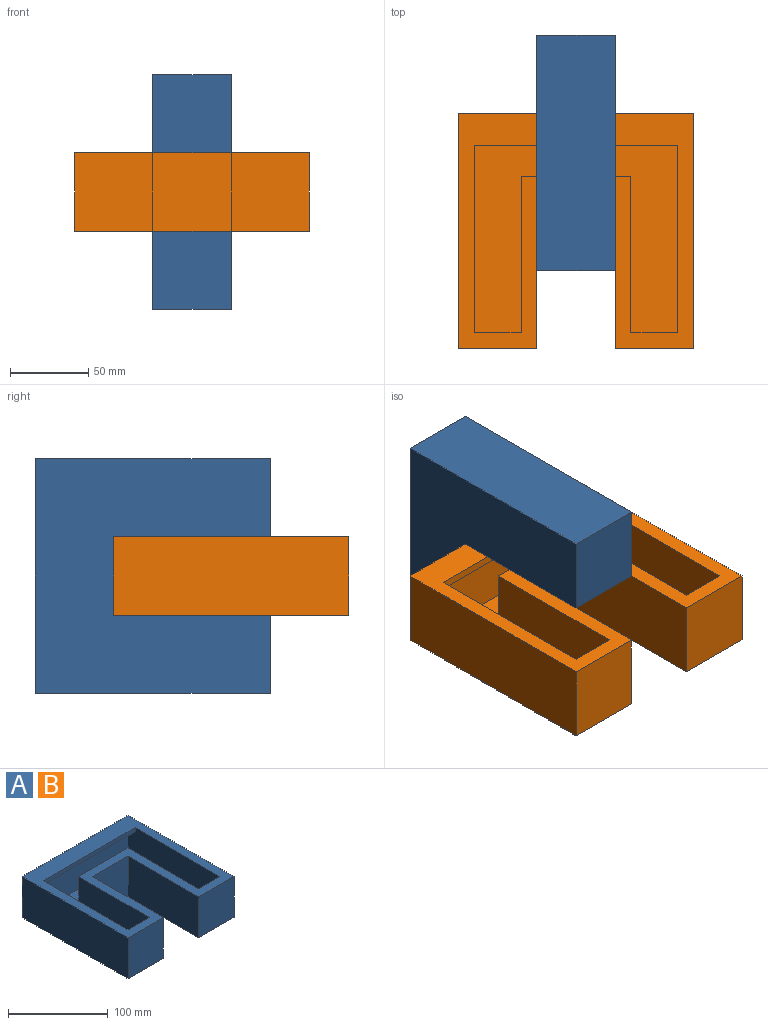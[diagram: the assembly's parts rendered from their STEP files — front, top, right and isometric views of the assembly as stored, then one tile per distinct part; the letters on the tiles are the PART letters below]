
ASSEMBLY  parts=2 mates=1
PART A: 21 faces, bbox 150x150x50 mm
  f0: plane 130x40mm, normal (0,-1,0), area 5200mm2, adj f1,f10,f18,f19
  f1: plane 130x45mm, normal (-1,0,0), area 5800mm2, adj f0,f11,f17,f18,f19,f20
  f2: plane 150x150mm, normal (0,0,-1), area 17500mm2, adj f3,f4,f5,f6,f7,f8,f9,f16
  f3: plane 150x50mm, normal (-1,0,0), area 7500mm2, adj f2,f4,f16,f17
  f4: plane 50x50mm, normal (0,-1,0), area 2500mm2, adj f2,f3,f5,f17
  f5: plane 100x50mm, normal (1,0,0), area 5000mm2, adj f2,f4,f6,f17
  f6: plane 50x50mm, normal (0,-1,0), area 2500mm2, adj f2,f5,f7,f17
  f7: plane 100x50mm, normal (-1,0,0), area 5000mm2, adj f2,f6,f8,f17
  f8: plane 50x50mm, normal (0,-1,0), area 2500mm2, adj f2,f7,f9,f17
  f9: plane 150x50mm, normal (1,0,0), area 7500mm2, adj f2,f8,f16,f17
  f10: plane 130x45mm, normal (1,0,0), area 5800mm2, adj f0,f15,f17,f18,f19,f20
  f11: plane 45x30mm, normal (0,1,0), area 1350mm2, adj f1,f12,f17,f18
  f12: plane 100x45mm, normal (1,0,0), area 4500mm2, adj f11,f13,f17,f18
  f13: plane 70x45mm, normal (0,1,0), area 3150mm2, adj f12,f14,f17,f18
  f14: plane 100x45mm, normal (-1,0,0), area 4500mm2, adj f13,f15,f17,f18
  f15: plane 45x30mm, normal (0,1,0), area 1350mm2, adj f10,f14,f17,f18
  f16: plane 150x50mm, normal (0,1,0), area 7500mm2, adj f2,f3,f9,f17
  f17: plane 150x150mm, normal (0,0,1), area 8900mm2, adj f1,f3,f4,f5,f6,f7,f8,f9
  f18: plane 130x130mm, normal (0,0,1), area 9900mm2, adj f0,f1,f10,f11,f12,f13,f14,f15
  f19: plane 130x10mm, normal (0,0,-1), area 1300mm2, adj f0,f1,f10,f20
  f20: plane 130x5mm, normal (0,-1,0), area 650mm2, adj f1,f10,f17,f19
PART B: same geometry as A
PLACE A rot(axis=(0,1,0),90deg) t=(-99.45,-41.44,-35.18)mm
PLACE B t=(0.55,-91.44,14.82)mm
MATE fastened A.f6 <-> B.f16  axis (0,-1,0) through (-74.45,58.56,39.82)mm
